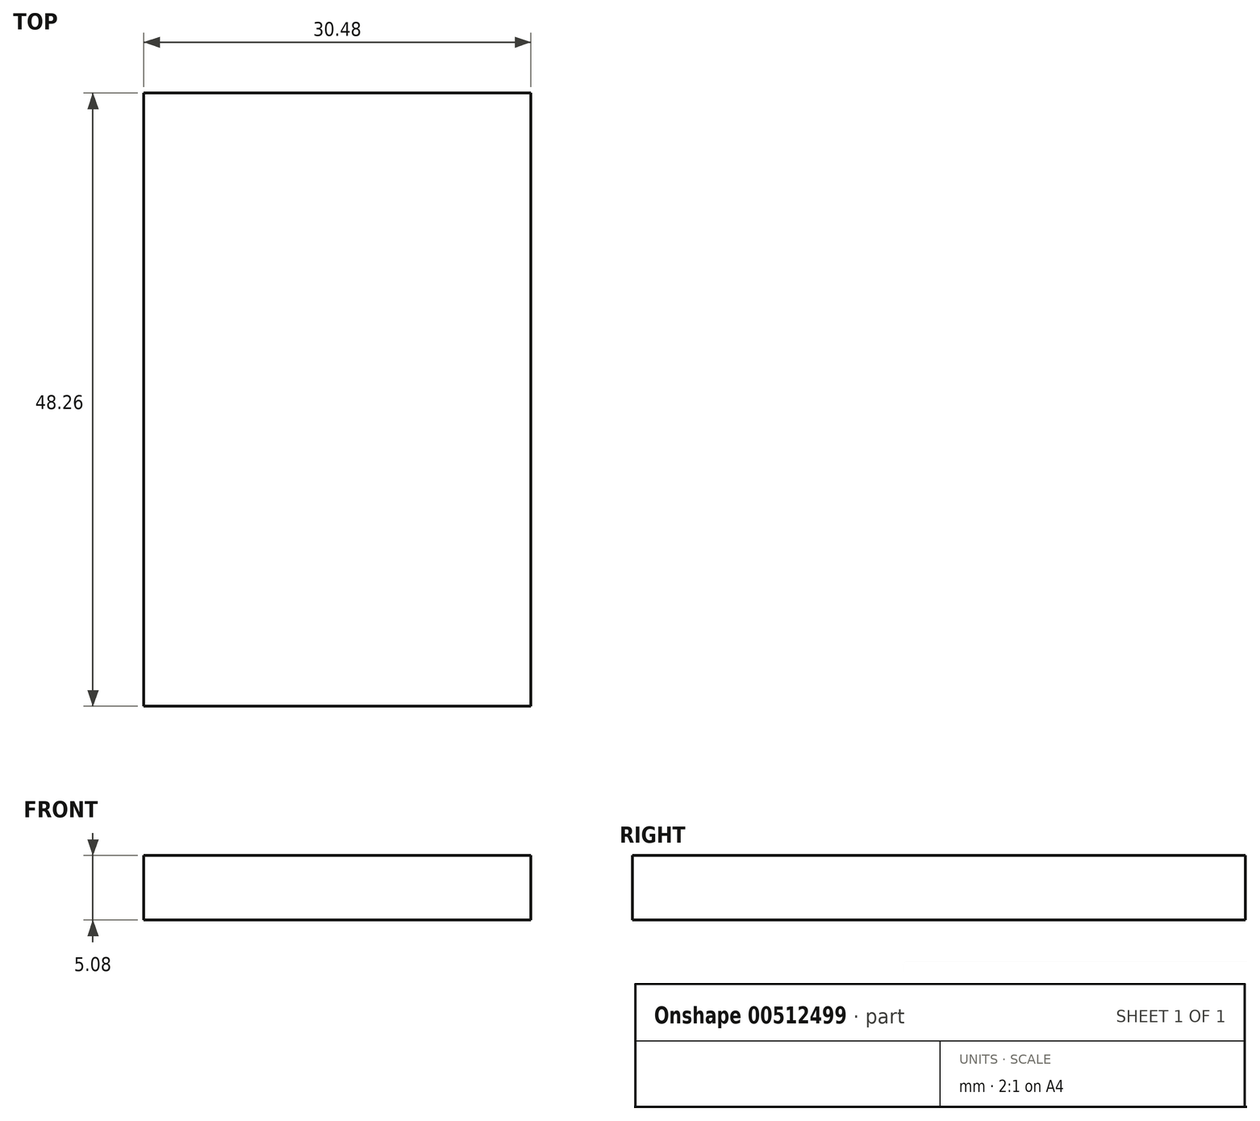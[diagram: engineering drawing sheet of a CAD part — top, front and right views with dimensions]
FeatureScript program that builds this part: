
annotation { "Feature Type Name" : "Feature", "Feature Type Description" : "" }
export const myFeature = defineFeature(function(context is Context, id is Id, definition is map)
    precondition{}
    {
        {
            var Q0;
            Q0=qCreatedBy(makeId("Top.planeOp"),FACE);
            var sketch = newSketch(context, id + "F0", { "sketchPlane" : qUnion([Q0])});
            skLineSegment(sketch, "E0.bottom", {"start": v(-37.06, -28.6) * mm, "end": v(-6.58, -28.6) * mm});
            skLineSegment(sketch, "E0.top", {"start": v(-37.06, 19.67) * mm, "end": v(-6.58, 19.67) * mm});
            skLineSegment(sketch, "E0.left", {"start": v(-37.06, -28.6) * mm, "end": v(-37.06, 19.67) * mm});
            skLineSegment(sketch, "E0.right", {"start": v(-6.58, -28.6) * mm, "end": v(-6.58, 19.67) * mm});
            skSolve(sketch);
        }
        {
            var Q0;
            Q0=makeQuery(id+"F0.imprint","IMPRINT",FACE,{"disambiguationData":[TD([[makeQuery(id+"F0.imprint","IMPRINT",EDGE,{"derivedFrom":sQuery(id+"F0.wireOp",EDGE,"E0.bottom")}),1.0]])]});
            extrude(context, id + "F1", {"entities" : qUnion([Q0]), "depth" : 5.08 * mm});
        }
    });
